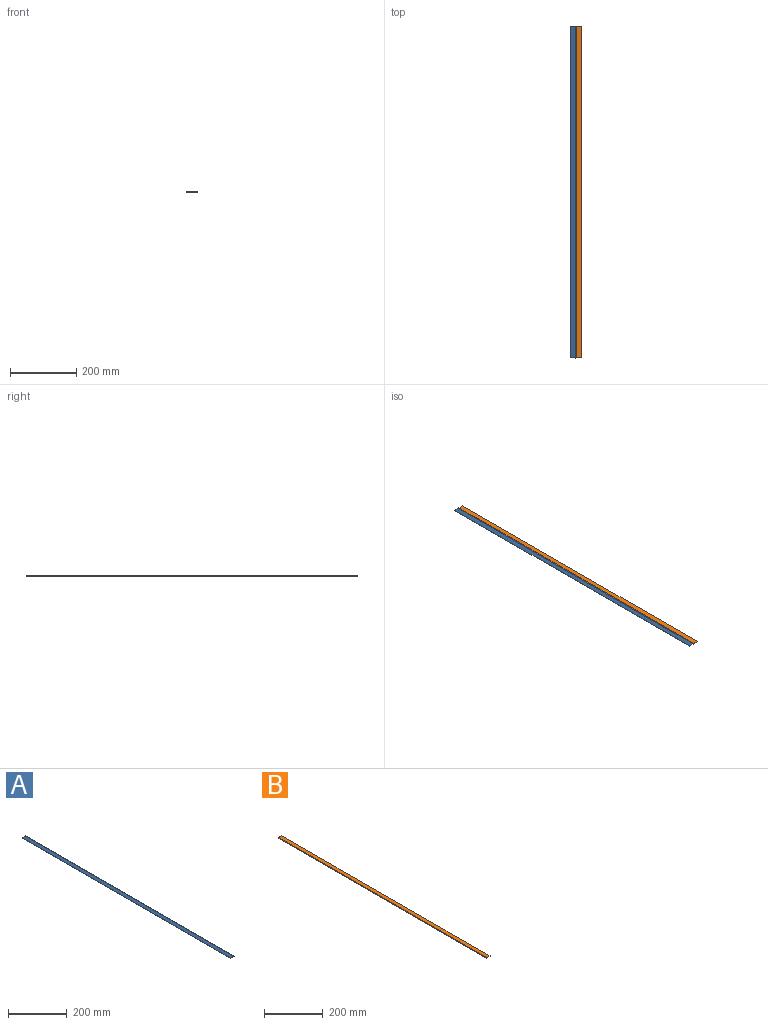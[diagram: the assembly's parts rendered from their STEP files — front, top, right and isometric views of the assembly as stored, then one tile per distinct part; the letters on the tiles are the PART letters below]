
ASSEMBLY  parts=2 mates=1
PART A: 6 faces, bbox 18x1000x3 mm
  f0: cylinder r=1.5mm len=1000mm, axis (0,1,0), area 8405.3mm2, adj f1,f2,f3,f4
  f1: plane 18x3mm, normal (0,-1,0), area 22.1mm2, adj f0,f3,f4,f5
  f2: plane 18x3mm, normal (0,1,0), area 22.1mm2, adj f0,f3,f4,f5
  f3: plane 1000x15.09mm, normal (0,0,1), area 15085.8mm2, adj f0,f1,f2,f5
  f4: plane 1000x15.09mm, normal (0,0,-1), area 15085.8mm2, adj f0,f1,f2,f5
  f5: plane 1000x1mm, normal (-1,0,0), area 1000mm2, adj f1,f2,f3,f4
PART B: 6 faces, bbox 18x1000x3 mm
  f0: cylinder r=1.5mm len=1000mm, axis (0,1,0), area 8405.3mm2, adj f1,f2,f3,f4
  f1: plane 18x3mm, normal (0,-1,0), area 22.1mm2, adj f0,f3,f4,f5
  f2: plane 18x3mm, normal (0,1,0), area 22.1mm2, adj f0,f3,f4,f5
  f3: plane 1000x15.09mm, normal (0,0,1), area 15085.8mm2, adj f0,f1,f2,f5
  f4: plane 1000x15.09mm, normal (0,0,-1), area 15085.8mm2, adj f0,f1,f2,f5
  f5: plane 1000x1mm, normal (1,0,0), area 1000mm2, adj f1,f2,f3,f4
PLACE A rot(axis=(1,0,0),0deg) t=(0,0,0)mm
PLACE B at identity fixed
MATE revolute A.f0 <-> B.f0  axis (0,1,0) through (0,0,0)mm
